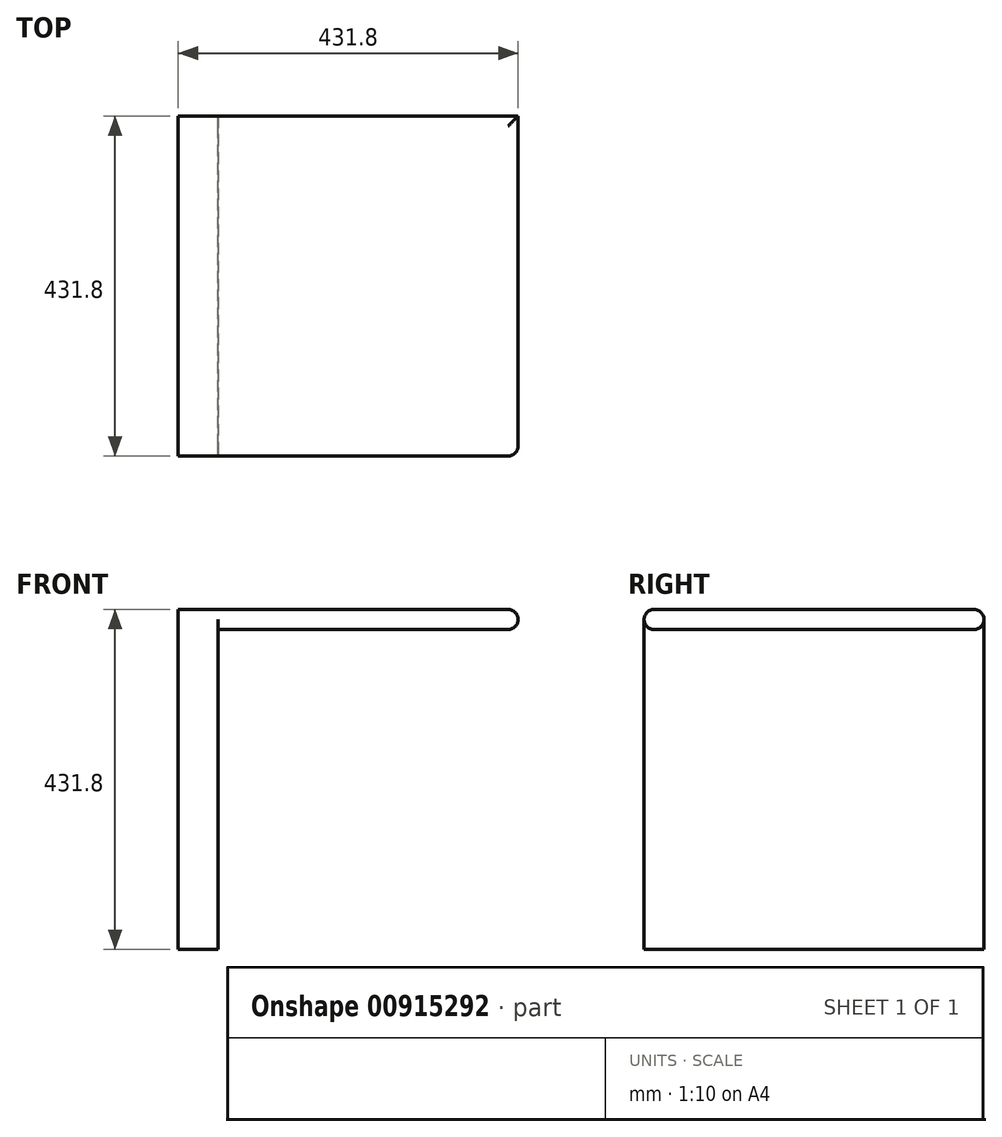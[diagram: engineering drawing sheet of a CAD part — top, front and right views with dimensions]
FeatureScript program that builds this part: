
annotation { "Feature Type Name" : "Feature", "Feature Type Description" : "" }
export const myFeature = defineFeature(function(context is Context, id is Id, definition is map)
    precondition{}
    {
        {
            var Q0;
            Q0=qCreatedBy(makeId("Right.planeOp"),FACE);
            var sketch = newSketch(context, id + "F0", { "sketchPlane" : qUnion([Q0])});
            skLineSegment(sketch, "E0.bottom", {"start": v(215.9, -215.9) * mm, "end": v(-215.9, -215.9) * mm});
            skLineSegment(sketch, "E0.top", {"start": v(215.9, 215.9) * mm, "end": v(-215.9, 215.9) * mm});
            skLineSegment(sketch, "E0.left", {"start": v(215.9, -215.9) * mm, "end": v(215.9, 215.9) * mm});
            skLineSegment(sketch, "E0.right", {"start": v(-215.9, -215.9) * mm, "end": v(-215.9, 215.9) * mm});
            skPoint(sketch, "E0.middle", {"position": v(0, 0) * mm});
            skLineSegment(sketch, "E1", {"start": v(-215.9, 190.5) * mm, "end": v(215.9, 190.5) * mm});
            skSolve(sketch);
        }
        {
            var Q0;
            {var subQ0=sQuery(id+"F0.wireOp",EDGE,"E0.top");Q0=makeQuery(id+"F0.imprint","IMPRINT",FACE,{"disambiguationData":[TD([[makeQuery(id+"F0.imprint","IMPRINT",EDGE,{"derivedFrom":subQ0}),1.0]])]});}
            extrude(context, id + "F1", {"entities" : qUnion([Q0]), "depth" : 431.8 * mm, "offsetDistance" : 25.4 * mm});
        }
        {
            var Q0;
            {var subQ0=sQuery(id+"F0.wireOp",EDGE,"E0.bottom");Q0=makeQuery(id+"F0.imprint","IMPRINT",FACE,{"disambiguationData":[TD([[makeQuery(id+"F0.imprint","IMPRINT",EDGE,{"derivedFrom":subQ0}),-1.0]])]});}
            extrude(context, id + "F2", {"entities" : qUnion([Q0]), "operationType" : NewBodyOperationType.ADD, "depth" : 50.8 * mm, "offsetDistance" : 25.4 * mm});
        }
        {
            var Q0;
            Q0=makeQuery(id+"F1.opExtrude","CAP_EDGE",EDGE,{"disambiguationData":[OSD([sQuery(id+"F0.wireOp",EDGE,"E1")])],"isStart":false});
            var Q1;
            Q1=makeQuery(id+"F1.opExtrude","CAP_EDGE",EDGE,{"disambiguationData":[OSD([sQuery(id+"F0.wireOp",EDGE,"E0.right")])],"isStart":false});
            var Q2;
            Q2=makeQuery(id+"F1.opExtrude","SWEPT_EDGE",EDGE,{"disambiguationData":[OSD([sQuery(id+"F0.wireOp",EDGE,"E0.right"),sQuery(id+"F0.wireOp",EDGE,"E1")])]});
            var Q3;
            Q3=makeQuery(id+"F1.opExtrude","SWEPT_EDGE",EDGE,{"disambiguationData":[OSD([sQuery(id+"F0.wireOp",EDGE,"E0.top"),sQuery(id+"F0.wireOp",EDGE,"E0.right")])]});
            var Q4;
            Q4=makeQuery(id+"F1.opExtrude","CAP_EDGE",EDGE,{"disambiguationData":[OSD([sQuery(id+"F0.wireOp",EDGE,"E0.top")])],"isStart":false});
            var Q5;
            Q5=makeQuery(id+"F1.opExtrude","SWEPT_EDGE",EDGE,{"disambiguationData":[OSD([sQuery(id+"F0.wireOp",EDGE,"E0.top"),sQuery(id+"F0.wireOp",EDGE,"E0.left")])]});
            var Q6;
            Q6=makeQuery(id+"F1.opExtrude","SWEPT_EDGE",EDGE,{"disambiguationData":[OSD([sQuery(id+"F0.wireOp",EDGE,"E0.left"),sQuery(id+"F0.wireOp",EDGE,"E1")])]});
            fillet(context, id + "F3", {"entities" : qUnion([Q0, Q1, Q2, Q3, Q4, Q5, Q6]), "radius" : 12.7 * mm, "tangentPropagation" : true, "allowEdgeOverflow" : false});
        }
    });
